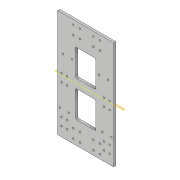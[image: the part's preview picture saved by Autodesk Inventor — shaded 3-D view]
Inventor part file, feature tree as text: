
AUTODESK INVENTOR PART (.ipt)
format: ipt  version: 2018 (Build 220112000, 112)  size: 212,992 bytes
history: native  units: in
note: dims shown in document units (in); Inventor stores cm internally (conversion verified against a paired STEP export)
features: reference x22, other x13, sketch x7, extrude x3, hole x3, fillet x2, plane x1, mirror x1, projected_geometry x1
ambient origin geometry x8: Origin, YZ Plane, XZ Plane, XY Plane, X Axis, Y Axis, Z Axis, Center Point
bodies: Solid1 (feature_tree)
feature tree (53):
  extrude  "Extrusion1"  Depth=12.0in
  sketch  "Sketch2"  dims[d2=0.25in d3=0.0in]
  hole  "Hole1"  [1 undecoded]
  hole  "Hole2"  [1 undecoded]
  plane  "Work Plane1"
  mirror  "Mirror1"
  extrude  "Extrusion2"  Depth=0.75in
  extrude  "Extrusion3"  Depth=1.0in
  fillet  "Fillet1"  Radius=0.75in
  fillet  "Fillet2"  Radius=1.0in
  hole  "Hole3"  [1 undecoded]
  sketch  "Sketch1"  dims[d0=6.25in d1=12.0in]
  reference  "Reference1"
  reference  "Reference2"
  reference  "Reference3"
  reference  "Reference4"
  reference  "Reference5"
  reference  "Reference6"
  reference  "Reference7"
  reference  "Reference8"
  reference  "Reference9"
  reference  "Reference10"
  reference  "Reference11"
  reference  "Reference12"
  reference  "Reference13"
  reference  "Reference14"
  reference  "Reference15"
  reference  "Reference16"
  reference  "Reference17"
  reference  "Reference18"
  reference  "Reference19"
  reference  "Reference20"
  reference  "Reference21"
  sketch  "Sketch3"  dims[d4=0.177in d5=0.75in d6=0.332in d7=0.25in d8=0.5635in d9=1.0in d10=0.8108in d11=0.75in]
  reference  "Reference22"
  sketch  "Sketch4"  dims[d12=0.75in d13=0.75in]
  projected_geometry  "Projected Loop1"
  sketch  "Sketch5"  dims[d14=0.75in d15=0.75in]
  sketch  "Sketch6"  dims[d16=0.75in d17=0.75in d18=0.75in d19=1.0in]
  sketch  "Sketch7"  dims[d20=1.0in d21=0.5in d22=0.5in d23=0.5in d24=0.5in d25=0.177in d26=0.75in d27=0.332in d28=0.25in d29=0.5635in d30=1.0in d31=0.8108in d32=2.5in d33=2.5in d34=2.0in d35=2.0in d36=0.25in d37=0.0in d38=0.5in d39=0.5in d40=0.125in d41=0.0in d42=0.125in d43=0.125in d44=1.0in d45=2.75in d46=2.75in d47=2.75in d48=2.75in d49=1.0in d50=0.25in d51=0.25in d52=0.177in d53=0.75in d54=0.332in d55=0.25in d56=0.5635in d57=1.0in d58=0.8108in]
  parser-record x1  (decoder bookkeeping rows leaked as tree rows — omitted from the tree; the rows remain in map.json)
  other  "Glyf bot.iam"
  other  "momotr mount 2:7"
  other  "momotr mount 2:6"
  other  "FTC Piv moount:8"
  other  "FTC Piv moount:5"
  other  "FTC Piv moount:6"
  other  "FTC Piv moount:7"
  other  "FTC Piv moount:3"
  other  "FTC Piv moount:1"
  other  "FTC Piv moount:4"
  other  "FTC Piv moount:2"
  other  "Drive Rail 1:1"
note: 3 required parameter values undecoded (feature->parameter linkage not recoverable at this tier; creation-order binding heuristic only, values carry confidence <= 0.55)
note: 1 file-system path scrubbed to <path> (originals preserved in map.json)
